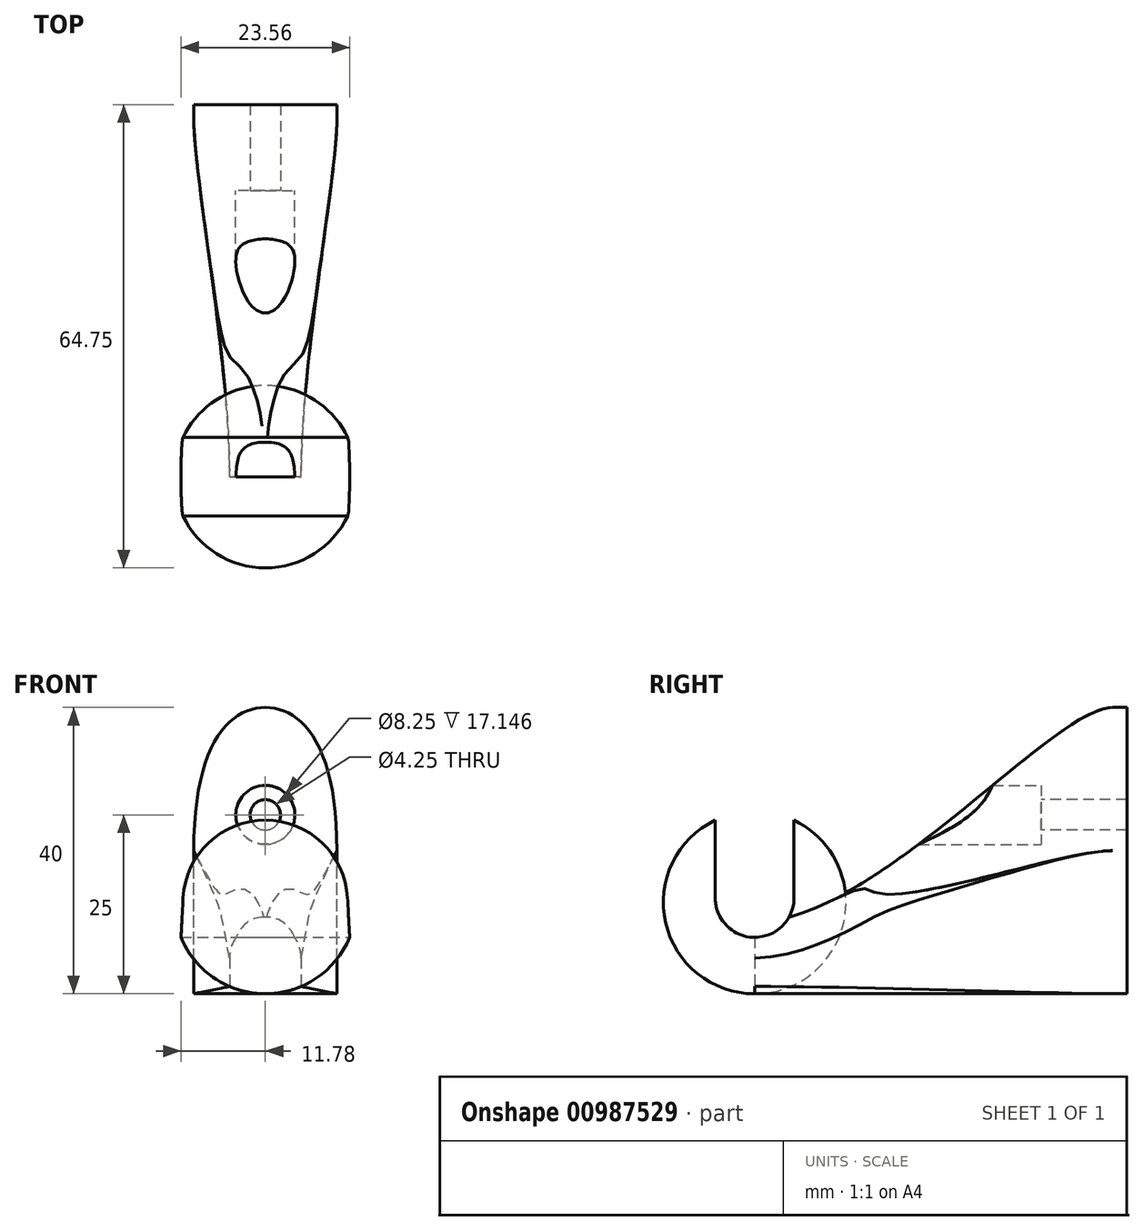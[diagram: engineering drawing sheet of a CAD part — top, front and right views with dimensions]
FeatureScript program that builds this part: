
annotation { "Feature Type Name" : "Feature", "Feature Type Description" : "" }
export const myFeature = defineFeature(function(context is Context, id is Id, definition is map)
    precondition{}
    {
        {
            var Q0;
            Q0=qCreatedBy(makeId("Right.planeOp"),FACE);
            var sketch = newSketch(context, id + "F0", { "sketchPlane" : qUnion([Q0])});
            skPoint(sketch, "E0.middle", {"position": v(0, 8.37) * mm});
            skPoint(sketch, "E1", {"position": v(-5.5, 8.37) * mm});
            skPoint(sketch, "E2", {"position": v(5.5, 8.37) * mm});
            skLineSegment(sketch, "E3.bottom", {"start": v(-5.5, 8.37) * mm, "end": v(5.5, 8.37) * mm, "construction": true});
            skLineSegment(sketch, "E3.top", {"start": v(-5.5, 21.72) * mm, "end": v(5.5, 21.72) * mm});
            skLineSegment(sketch, "E3.left", {"start": v(-5.5, 8.37) * mm, "end": v(-5.5, 21.72) * mm});
            skLineSegment(sketch, "E3.right", {"start": v(5.5, 8.37) * mm, "end": v(5.5, 21.72) * mm});
            skArc(sketch, "E4", {"start": v(-5.5, 8.37) * mm, "mid": v(0, 2.87) * mm, "end": v(5.5, 8.37) * mm});
            skArc(sketch, "E5", {"start": v(5.5, 8.37) * mm, "mid": v(0, 13.87) * mm, "end": v(-5.5, 8.37) * mm, "construction": true});
            skSolve(sketch);
        }
        {
            var Q0;
            Q0=qCreatedBy(makeId("Front.planeOp"),FACE);
            cPlane(context, id + "F1", {"entities" : qUnion([Q0]), "cplaneType" : CPlaneType.OFFSET, "offset" : 50 * mm, "oppositeDirection" : true, "width" : 150 * mm, "height" : 150 * mm});
        }
        {
            var Q0;
            Q0=qCreatedBy(makeId("Front.planeOp"),FACE);
            var sketch = newSketch(context, id + "F2", { "sketchPlane" : qUnion([Q0])});
            skLineSegment(sketch, "E6.bottom", {"start": v(-5, 5) * mm, "end": v(5, 5) * mm});
            skLineSegment(sketch, "E6.top", {"start": v(-5, -5) * mm, "end": v(5, -5) * mm});
            skLineSegment(sketch, "E6.left", {"start": v(-5, 5) * mm, "end": v(-5, -5) * mm});
            skLineSegment(sketch, "E6.right", {"start": v(5, 5) * mm, "end": v(5, -5) * mm});
            skPoint(sketch, "E6.middle", {"position": v(0, 0) * mm});
            skPoint(sketch, "E7", {"position": v(0, 5) * mm});
            skArc(sketch, "E8", {"start": v(0, 20.5) * mm, "mid": v(12.75, 7.75) * mm, "end": v(0, -5) * mm});
            skLineSegment(sketch, "E9", {"start": v(0, 20.5) * mm, "end": v(0, -5) * mm});
            skArc(sketch, "E10.MirrorCS", {"start": v(0, 20.5) * mm, "mid": v(-12.75, 7.75) * mm, "end": v(0, -5) * mm});
            skSolve(sketch);
        }
        {
            var Q0;
            Q0=qCreatedBy(id+"F1.planeOp",FACE);
            var sketch = newSketch(context, id + "F3", { "sketchPlane" : qUnion([Q0])});
            skLineSegment(sketch, "E11.bottom", {"start": v(-10, -5) * mm, "end": v(0, -5) * mm});
            skLineSegment(sketch, "E11.top", {"start": v(-10, 35) * mm, "end": v(10, 35) * mm});
            skLineSegment(sketch, "E11.left", {"start": v(-10, -5) * mm, "end": v(-10, 35) * mm});
            skLineSegment(sketch, "E11.right", {"start": v(10, -5) * mm, "end": v(10, 35) * mm});
            skFitSpline(sketch, "E12", {"points": [v(-10, 15) * mm, v(0, 35) * mm, v(10, 15) * mm], "startDerivative": vector(0, 90) * mm, "endDerivative": vector(0, -90) * mm});
            skLineSegment(sketch, "E13", {"start": v(0, -5) * mm, "end": v(10, -5) * mm});
            skSolve(sketch);
        }
        {
            var Q0;
            {var subQ4=sQuery(id+"F3.wireOp",EDGE,"E11.bottom");Q0=makeQuery(id+"F3.imprint","IMPRINT",FACE,{"disambiguationData":[TD([[makeQuery(id+"F3.imprint","IMPRINT",EDGE,{"derivedFrom":subQ4}),1.0]])]});}
            var Q1;
            Q1=makeQuery(id+"F2.imprint","IMPRINT",FACE,{"disambiguationData":[TD([[makeQuery(id+"F2.imprint","IMPRINT",EDGE,{"derivedFrom":sQuery(id+"F2.wireOp",EDGE,"E6.bottom")}),-1.0]])]});
            var Q2;
            Q2=sQuery(id+"F3.wireOp",VERTEX,"E12.1.internal");
            var Q3;
            Q3=sQuery(id+"F2.wireOp",VERTEX,"E7");
            loft(context, id + "F4", {"startCondition" : LoftEndDerivativeType.NORMAL_TO_PROFILE, "startMagnitude" : .5, "endCondition" : LoftEndDerivativeType.NORMAL_TO_PROFILE, "endMagnitude" : 1, "sheetProfilesArray" : [{ "sheetProfileEntities" : qUnion([Q0]) }, { "sheetProfileEntities" : qUnion([Q1]) }], "matchConnections" : true, "connections" : [{ "connectionEntities" : qUnion([Q2, Q3]), "connectionEdgeQueries" : qUnion([]), "connectionEdgeParameters" : [] }]});
        }
        {
            var Q0;
            {var subQ4=sQuery(id+"F3.wireOp",EDGE,"E11.bottom");Q0=makeQuery(id+"F3.imprint","IMPRINT",FACE,{"disambiguationData":[TD([[makeQuery(id+"F3.imprint","IMPRINT",EDGE,{"derivedFrom":subQ4}),1.0]])]});}
            extrude(context, id + "F5", {"entities" : qUnion([Q0]), "operationType" : NewBodyOperationType.ADD, "oppositeDirection" : true, "depth" : 2 * mm, "offsetDistance" : 25 * mm});
        }
        {
            var Q0;
            {var subQ0=sQuery(id+"F2.wireOp",EDGE,"E6.right");var subQ1=sQuery(id+"F2.wireOp",EDGE,"E6.bottom");var subQ2=makeQuery(id+"F2.imprint","INTERSECT",VERTEX,{"derivedFrom":[subQ1,subQ0]});Q0=makeQuery(id+"F2.imprint","IMPRINT",FACE,{"disambiguationData":[TD([[makeQuery(id+"F2.imprint","IMPRINT",EDGE,{"disambiguationData":[TD([[subQ2,1.0]])],"derivedFrom":subQ1}),1.0]])]});}
            var Q1;
            {var subQ0=sQuery(id+"F2.wireOp",EDGE,"E6.right");var subQ1=sQuery(id+"F2.wireOp",EDGE,"E6.bottom");var subQ2=makeQuery(id+"F2.imprint","INTERSECT",VERTEX,{"derivedFrom":[subQ1,subQ0]});Q1=makeQuery(id+"F2.imprint","IMPRINT",FACE,{"disambiguationData":[TD([[makeQuery(id+"F2.imprint","IMPRINT",EDGE,{"disambiguationData":[TD([[subQ2,1.0]])],"derivedFrom":subQ1}),-1.0]])]});}
            var Q2;
            Q2=sQuery(id+"F2.wireOp",EDGE,"E9");
            revolve(context, id + "F6", {"surfaceOperationType" : NewSurfaceOperationType.NEW, "entities" : qUnion([Q0, Q1]), "axis" : qUnion([Q2]), "revolveType" : RevolveType.FULL});
        }
        {
            var Q0;
            Q0=makeQuery(id+"F0.imprint","IMPRINT",FACE,{"disambiguationData":[TD([[makeQuery(id+"F0.imprint","IMPRINT",EDGE,{"derivedFrom":sQuery(id+"F0.wireOp",EDGE,"E3.top")}),-1.0]])]});
            extrude(context, id + "F7", {"entities" : qUnion([Q0]), "operationType" : NewBodyOperationType.REMOVE, "endBound" : BoundingType.SYMMETRIC, "oppositeDirection" : true, "depth" : 30 * mm, "offsetDistance" : 25 * mm});
        }
        {
            var Q0;
            {var subQ4=sQuery(id+"F3.wireOp",EDGE,"E11.bottom");Q0=makeQuery(id+"F3.imprint","IMPRINT",FACE,{"disambiguationData":[TD([[makeQuery(id+"F3.imprint","IMPRINT",EDGE,{"derivedFrom":subQ4}),1.0]])]});}
            cPlane(context, id + "F8", {"entities" : qUnion([Q0]), "cplaneType" : CPlaneType.OFFSET, "offset" : 10 * mm, "width" : 150 * mm, "height" : 150 * mm});
        }
        {
            var Q0;
            Q0=qCreatedBy(id+"F8.planeOp",FACE);
            var sketch = newSketch(context, id + "F9", { "sketchPlane" : qUnion([Q0])});
            skCircle(sketch, "E14", {"center": v(0, 20) * mm, "radius": 2.12 * mm});
            skCircle(sketch, "E15", {"center": v(0, 20) * mm, "radius": 4.12 * mm});
            skSolve(sketch);
        }
        {
            var Q0;
            Q0=makeQuery(id+"F9.imprint","IMPRINT",FACE,{"disambiguationData":[TD([[makeQuery(id+"F9.imprint","IMPRINT",EDGE,{"derivedFrom":sQuery(id+"F9.wireOp",EDGE,"E14")}),1.0]])]});
            var Q1;
            Q1=makeQuery(id+"F9.imprint","IMPRINT",FACE,{"disambiguationData":[TD([[makeQuery(id+"F9.imprint","IMPRINT",EDGE,{"derivedFrom":sQuery(id+"F9.wireOp",EDGE,"E14")}),-1.0]])]});
            extrude(context, id + "F10", {"entities" : qUnion([Q0, Q1]), "operationType" : NewBodyOperationType.REMOVE, "depth" : 20 * mm, "offsetDistance" : 25 * mm});
        }
        {
            var Q0;
            Q0=makeQuery(id+"F9.imprint","IMPRINT",FACE,{"disambiguationData":[TD([[makeQuery(id+"F9.imprint","IMPRINT",EDGE,{"derivedFrom":sQuery(id+"F9.wireOp",EDGE,"E14")}),1.0]])]});
            extrude(context, id + "F11", {"entities" : qUnion([Q0]), "operationType" : NewBodyOperationType.REMOVE, "oppositeDirection" : true, "depth" : 15 * mm, "offsetDistance" : 25 * mm});
        }
        {
            var Q0;
            Q0=makeQuery(id+"F4.opLoft","SWEPT_EDGE",EDGE,{"disambiguationData":[OSD([sQuery(id+"F2.wireOp",EDGE,"E6.bottom"),sQuery(id+"F2.wireOp",EDGE,"E6.right"),sQuery(id+"F3.wireOp",EDGE,"E11.right"),sQuery(id+"F3.wireOp",EDGE,"E12")])]});
            var Q1;
            Q1=makeQuery(id+"F4.opLoft","SWEPT_EDGE",EDGE,{"disambiguationData":[OSD([sQuery(id+"F2.wireOp",EDGE,"E6.bottom"),sQuery(id+"F2.wireOp",EDGE,"E6.left"),sQuery(id+"F3.wireOp",EDGE,"E11.left"),sQuery(id+"F3.wireOp",EDGE,"E12")])]});
            fillet(context, id + "F12", {"entities" : qUnion([Q0, Q1]), "radius" : 5 * mm, "tangentPropagation" : true, "allowEdgeOverflow" : false});
        }
    });
